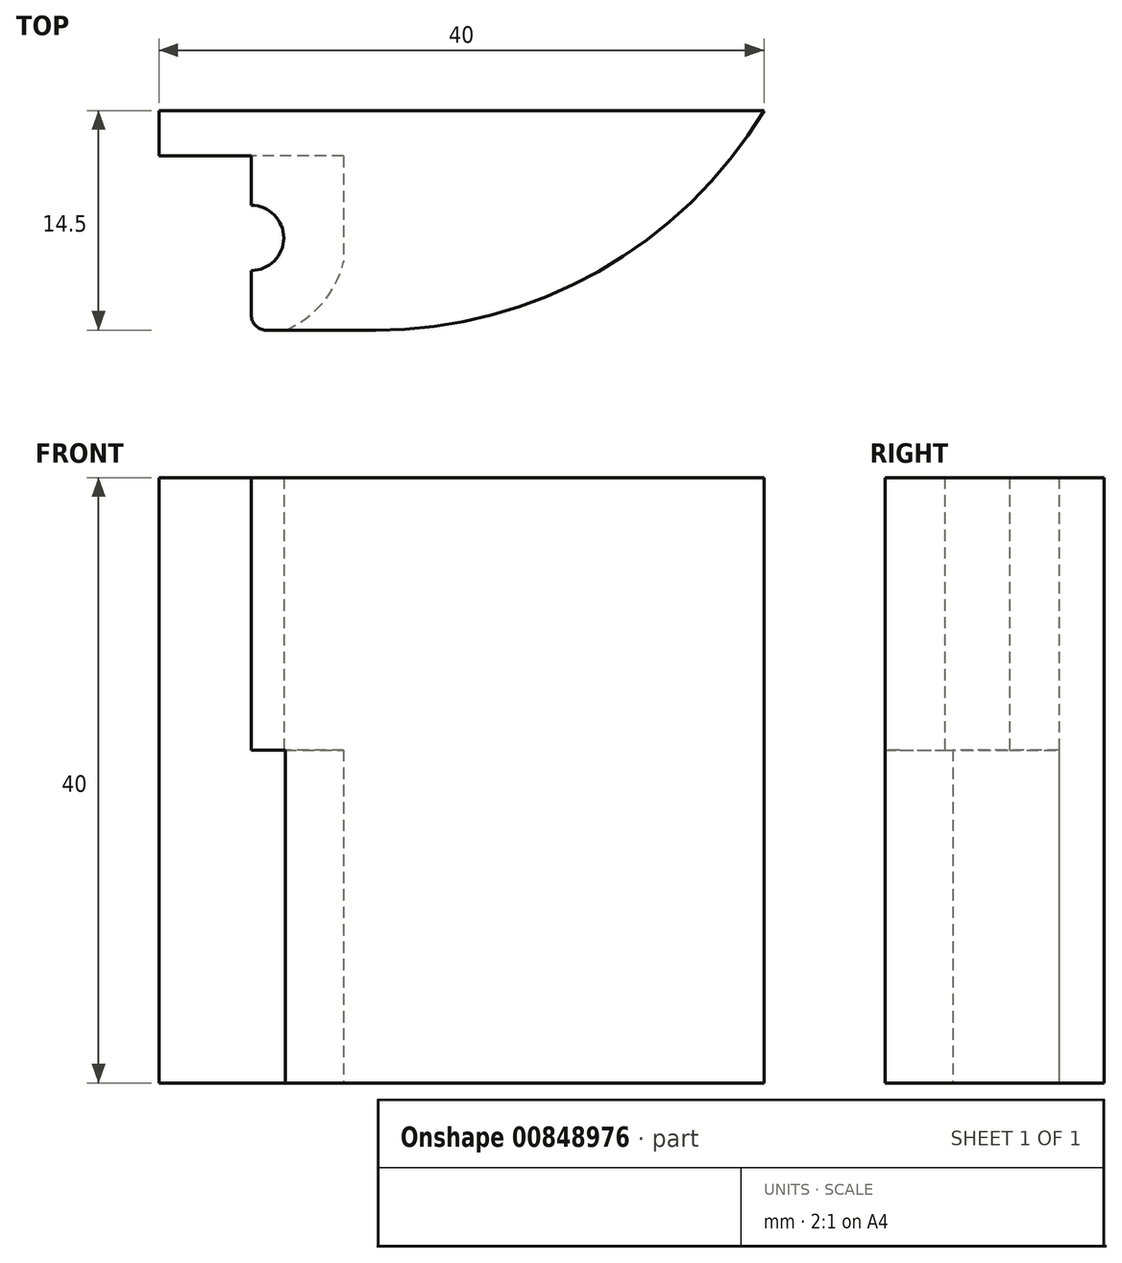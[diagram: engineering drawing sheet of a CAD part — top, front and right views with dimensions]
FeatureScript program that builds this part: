
annotation { "Feature Type Name" : "Feature", "Feature Type Description" : "" }
export const myFeature = defineFeature(function(context is Context, id is Id, definition is map)
    precondition{}
    {
        {
            var Q0;
            Q0=qCreatedBy(makeId("Top.planeOp"),FACE);
            var sketch = newSketch(context, id + "F0", { "sketchPlane" : qUnion([Q0])});
            skLineSegment(sketch, "E0.bottom", {"start": v(6.1, 8.41) * mm, "end": v(-6.1, 8.41) * mm});
            skLineSegment(sketch, "E0.left", {"start": v(6.1, 8.41) * mm, "end": v(6.1, -1.59) * mm});
            skLineSegment(sketch, "E0.right", {"start": v(-6.1, 8.41) * mm, "end": v(-6.1, -1.59) * mm});
            skArc(sketch, "E1", {"start": v(-6.1, -1.59) * mm, "mid": v(-4.7, -4.3) * mm, "end": v(-2.25, -6.09) * mm});
            skLineSegment(sketch, "E2", {"start": v(-2.25, -6.1) * mm, "end": v(0, -6.1) * mm});
            skArc(sketch, "E3.MirrorCS", {"start": v(6.1, -1.59) * mm, "mid": v(4.7, -4.3) * mm, "end": v(2.25, -6.09) * mm});
            skLineSegment(sketch, "E4.MirrorCS", {"start": v(2.25, -6.09) * mm, "end": v(0, -6.1) * mm});
            skCircle(sketch, "E5", {"center": v(0, 0) * mm, "radius": 2.15 * mm});
            skLineSegment(sketch, "E6.bottom", {"start": v(0, -6.1) * mm, "end": v(33.9, -6.1) * mm});
            skLineSegment(sketch, "E6.top", {"start": v(0, 8.41) * mm, "end": v(33.9, 8.41) * mm});
            skLineSegment(sketch, "E6.left", {"start": v(0, -6.1) * mm, "end": v(0, 8.41) * mm});
            skLineSegment(sketch, "E6.right", {"start": v(33.9, -6.1) * mm, "end": v(33.9, 8.41) * mm});
            skLineSegment(sketch, "E7.bottom", {"start": v(33.9, 8.41) * mm, "end": v(-6.1, 8.41) * mm});
            skLineSegment(sketch, "E7.top", {"start": v(33.9, 5.41) * mm, "end": v(-6.1, 5.41) * mm});
            skLineSegment(sketch, "E7.left", {"start": v(33.9, 8.41) * mm, "end": v(33.9, 5.41) * mm});
            skLineSegment(sketch, "E7.right", {"start": v(-6.1, 8.41) * mm, "end": v(-6.1, 5.41) * mm});
            skSolve(sketch);
        }
        {
            var Q0;
            Q0=makeQuery(id+"F0.imprint","IMPRINT",FACE,{"disambiguationData":[TD([[makeQuery(id+"F0.imprint","IMPRINT",EDGE,{"derivedFrom":sQuery(id+"F0.wireOp",EDGE,"E0.bottom")}),1.0]])]});
            var Q1;
            {var subQ7=sQuery(id+"F0.wireOp",EDGE,"E0.left");Q1=makeQuery(id+"F0.imprint","IMPRINT",FACE,{"disambiguationData":[TD([[makeQuery(id+"F0.imprint","IMPRINT",EDGE,{"derivedFrom":subQ7}),-1.0]])]});}
            var Q2;
            {var subQ4=sQuery(id+"F0.wireOp",EDGE,"E0.left");Q2=makeQuery(id+"F0.imprint","IMPRINT",FACE,{"disambiguationData":[TD([[makeQuery(id+"F0.imprint","IMPRINT",EDGE,{"derivedFrom":subQ4}),1.0]])]});}
            var Q3;
            {var subQ5=sQuery(id+"F0.wireOp",EDGE,"E7.right");Q3=makeQuery(id+"F0.imprint","IMPRINT",FACE,{"disambiguationData":[TD([[makeQuery(id+"F0.imprint","IMPRINT",EDGE,{"derivedFrom":subQ5}),1.0]])]});}
            var Q4;
            {var subQ5=sQuery(id+"F0.wireOp",EDGE,"E0.right");Q4=makeQuery(id+"F0.imprint","IMPRINT",FACE,{"disambiguationData":[TD([[makeQuery(id+"F0.imprint","IMPRINT",EDGE,{"derivedFrom":subQ5}),1.0]])]});}
            var Q5;
            {var subQ2=sQuery(id+"F0.wireOp",EDGE,"E3.MirrorCS");Q5=makeQuery(id+"F0.imprint","IMPRINT",FACE,{"disambiguationData":[TD([[makeQuery(id+"F0.imprint","IMPRINT",EDGE,{"derivedFrom":subQ2}),1.0]])]});}
            var Q6;
            {var subQ3=sQuery(id+"F0.wireOp",EDGE,"E3.MirrorCS");Q6=makeQuery(id+"F0.imprint","IMPRINT",FACE,{"disambiguationData":[TD([[makeQuery(id+"F0.imprint","IMPRINT",EDGE,{"derivedFrom":subQ3}),-1.0]])]});}
            extrude(context, id + "F1", {"entities" : qUnion([Q0, Q1, Q2, Q3, Q4, Q5, Q6]), "depth" : 40 * mm, "offsetDistance" : 25 * mm});
        }
        {
            var Q0;
            Q0=makeQuery(id+"F1.opExtrude","SWEPT_EDGE",EDGE,{"disambiguationData":[OSD([sQuery(id+"F0.wireOp",EDGE,"E1"),sQuery(id+"F0.wireOp",EDGE,"E2")])]});
            var Q1;
            Q1=makeQuery(id+"F1.opExtrude","SWEPT_EDGE",EDGE,{"disambiguationData":[OSD([sQuery(id+"F0.wireOp",EDGE,"E3.MirrorCS"),sQuery(id+"F0.wireOp",EDGE,"E4.MirrorCS")])]});
            fillet(context, id + "F2", {"entities" : qUnion([Q0, Q1]), "radius" : 1 * mm, "tangentPropagation" : true, "allowEdgeOverflow" : false});
        }
        {
            var Q0;
            Q0=makeQuery(id+"F1.opExtrude","SWEPT_EDGE",EDGE,{"disambiguationData":[OSD([sQuery(id+"F0.wireOp",EDGE,"E6.bottom"),sQuery(id+"F0.wireOp",EDGE,"E6.right")])]});
            fillet(context, id + "F3", {"entities" : qUnion([Q0]), "radius" : 30 * mm, "tangentPropagation" : true, "allowEdgeOverflow" : false});
        }
        {
            var Q0;
            {var subQ5=sQuery(id+"F0.wireOp",EDGE,"E7.right");Q0=makeQuery(id+"F0.imprint","IMPRINT",FACE,{"disambiguationData":[TD([[makeQuery(id+"F0.imprint","IMPRINT",EDGE,{"derivedFrom":subQ5}),1.0]])]});}
            var Q1;
            {var subQ0=sQuery(id+"F0.wireOp",EDGE,"E7.bottom");var subQ1=sQuery(id+"F0.wireOp",EDGE,"E0.left");var subQ2=makeQuery(id+"F0.imprint","INTERSECT",VERTEX,{"derivedFrom":[subQ1,subQ0]});Q1=makeQuery(id+"F0.imprint","IMPRINT",FACE,{"disambiguationData":[TD([[makeQuery(id+"F0.imprint","IMPRINT",EDGE,{"disambiguationData":[TD([[subQ2,-1.0]])],"derivedFrom":subQ1}),-1.0]])]});}
            var Q2;
            {var subQ5=sQuery(id+"F0.wireOp",EDGE,"E7.left");Q2=makeQuery(id+"F0.imprint","IMPRINT",FACE,{"disambiguationData":[TD([[makeQuery(id+"F0.imprint","IMPRINT",EDGE,{"derivedFrom":subQ5}),-1.0]])]});}
            extrude(context, id + "F4", {"entities" : qUnion([Q0, Q1, Q2]), "operationType" : NewBodyOperationType.REMOVE, "oppositeDirection" : true, "depth" : -22 * mm, "offsetDistance" : 25 * mm});
        }
    });
